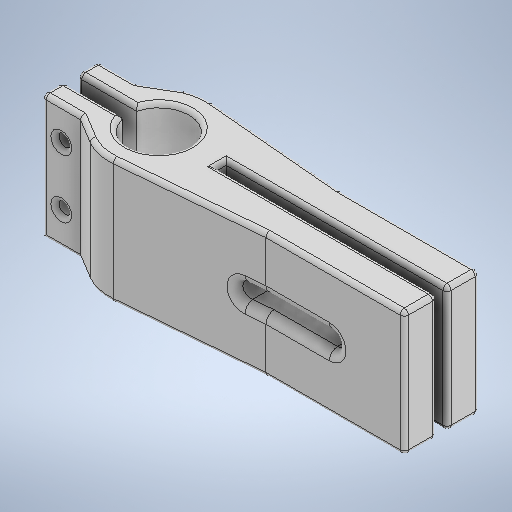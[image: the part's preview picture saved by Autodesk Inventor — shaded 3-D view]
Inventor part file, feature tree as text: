
AUTODESK INVENTOR PART (.ipt)
format: ipt  version: 2025.1 (Build 291241000, 241)  size: 922,112 bytes
history: native  units: mm
features: extrude x2, fillet x2, sketch x2
ambient origin geometry x8: Origin, YZ Plane, XZ Plane, XY Plane, X Axis, Y Axis, Z Axis, Center Point
bodies: Solide1 (feature_tree)
feature tree (6):
  extrude  "Extrusion1"  Depth=14.5mm
  extrude  "Extrusion2"  Depth=24.0mm
  fillet  "Congé1"  Radius=3.5mm
  fillet  "Congé2"  Radius=14.0mm
  sketch  "Esquisse1"
  sketch  "Esquisse2"
